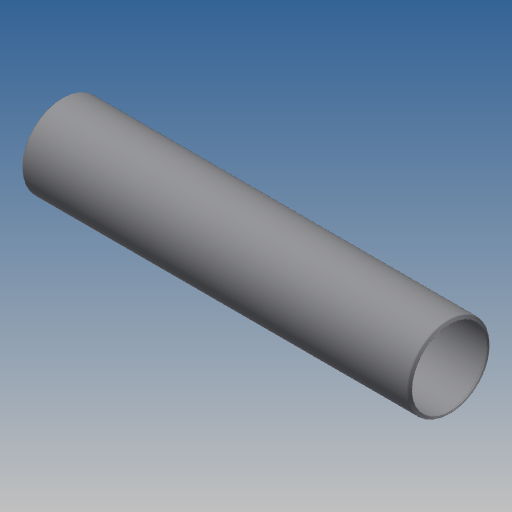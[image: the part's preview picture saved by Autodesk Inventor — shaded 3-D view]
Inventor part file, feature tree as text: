
AUTODESK INVENTOR PART (.ipt)
format: ipt  version: 2020 (Build 240168000, 168)  size: 159,744 bytes
history: native  units: in
note: dims shown in document units (in); Inventor stores cm internally (conversion verified against a paired STEP export)
features: other x42, revolve x1, sketch x1
ambient origin geometry x8: Origin, YZ Plane, XZ Plane, XY Plane, X Axis, Y Axis, Z Axis, Center Point
bodies: Solid1 (feature_tree)
feature tree (44):
  revolve  "Revolution1"  [1 undecoded]
  other  "cp1_XY"
  other  "cp1_YZ"
  other  "cp1_ZX"
  other  "cp1_X"
  other  "cp1_Y"
  other  "cp1_Z"
  other  "cp1_Center"
  other  "cp2_XY"
  other  "cp2_YZ"
  other  "cp2_ZX"
  other  "cp2_X"
  other  "cp2_Y"
  other  "cp2_Z"
  other  "cp2_Center"
  other  "cp3_XY"
  other  "cp3_YZ"
  other  "cp3_ZX"
  other  "cp3_X"
  other  "cp3_Y"
  other  "cp3_Z"
  other  "cp3_Center"
  other  "cp4_XY"
  other  "cp4_YZ"
  other  "cp4_ZX"
  other  "cp4_X"
  other  "cp4_Y"
  other  "cp4_Z"
  other  "cp4_Center"
  other  "tube_front_XY"
  other  "tube_front_YZ"
  other  "tube_front_ZX"
  other  "tube_front_X"
  other  "tube_front_Y"
  other  "tube_front_Z"
  other  "tube_front_Center"
  other  "tube_rear_XY"
  other  "tube_rear_YZ"
  other  "tube_rear_ZX"
  other  "tube_rear_X"
  other  "tube_rear_Y"
  other  "tube_rear_Z"
  other  "tube_rear_Center"
  sketch  "Sketch_1"  dims[d0=360.0deg]
note: 1 required parameter value undecoded (feature->parameter linkage not recoverable at this tier; creation-order binding heuristic only, values carry confidence <= 0.55)
